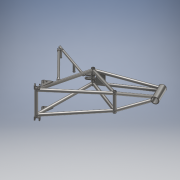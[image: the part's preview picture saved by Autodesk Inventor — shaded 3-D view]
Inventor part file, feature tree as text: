
AUTODESK INVENTOR PART (.ipt)
format: ipt  version: 2018 (Build 220112000, 112)  size: 1,016,832 bytes
history: native  units: mm
features: other x19, sketch x15, extrude x13, plane x10, loft x3, boolean_combine x2, thicken_offset x2, shell x1, mirror x1, hole x1, projected_geometry x1
ambient origin geometry x8: Origin, YZ Plane, XZ Plane, XY Plane, X Axis, Y Axis, Z Axis, Center Point
bodies: Solid8 (feature_tree), Solid1 (feature_tree), Solid16 (feature_tree), Solid17 (feature_tree), Solid18 (feature_tree), Solid19 (feature_tree), Solid20 (feature_tree), Solid24 (feature_tree)
feature tree (68):
  other  "MainFrame.ipt"
  plane  "Work Plane1"
  extrude  "Extrusion1"  Depth=10.0mm
  sketch  "3D Sketch3"
  plane  "Work Plane4"
  extrude  "Extrusion2"  Depth=13.0mm
  plane  "Work Plane5"
  extrude  "Extrusion4"  Depth=3.5mm
  loft  "Loft1"
  plane  "Work Plane2"
  extrude  "Extrusion5"  Depth=10.0mm TaperAngle=0.0deg
  extrude  "Extrusion6"  Depth=18.0mm TaperAngle=0.0deg
  shell  "Shell1"  Thickness=0.0mm
  plane  "Work Plane6"
  extrude  "Extrusion7"  Depth=5.0mm
  sketch  "3D Sketch4"
  plane  "Work Plane7"
  plane  "Work Plane8"
  plane  "Work Plane9"
  plane  "Work Plane11"
  extrude  "Extrusion8"  Depth=4.0mm TaperAngle=0.0deg
  extrude  "Extrusion9"  Depth=1.2mm
  extrude  "Extrusion10"  Depth=20.0mm
  loft  "Loft2"
  loft  "Loft3"
  extrude  "Extrusion13"  Depth=4.0mm TaperAngle=0.0deg
  extrude  "Extrusion15"  Depth=4.0mm TaperAngle=0.0deg
  mirror  "Mirror4"
  sketch  "Sketch17"  dims[d37=13.0mm d38=5.0mm d39=3.5mm d40=4.5mm d41=0.0mm d42=20.0mm]
  plane  "Work Plane13"
  sketch  "Sketch20"  dims[d43=20.0mm d44=-10.0mm d45=10.0mm]
  extrude  "Extrusion17"  Depth=4.0mm
  hole  "Hole3"  [1 undecoded]
  boolean_combine  "Combine2"
  thicken_offset  "Thicken2"
  extrude  "Extrusion19"  Depth=4.0mm TaperAngle=0.0deg
  boolean_combine  "Combine4"
  thicken_offset  "Thicken4"
  other  "Frame::MainFrame.ipt"
  other  "TaggingFeature1"
  sketch  "Sketch1"  dims[d0=10.0mm d1=50.0mm]
  other  "PlateA"
  sketch  "Sketch3"  dims[d2=37.0mm d3=13.0mm]
  sketch  "Sketch4"  dims[d4=5.0mm d5=3.5mm]
  other  "Edges1"
  other  "Edges2"
  sketch  "Sketch5"  dims[d6=4.4mm d7=0.0mm d8=20.0mm]
  other  "PlateB"
  sketch  "Sketch6"  dims[d11=15.875mm d13=10.0mm d14=0.0mm]
  sketch  "Sketch8"  dims[d15=-10.0mm d18=18.0mm d19=0.0mm d20=0.0mm d21=90.0deg]
  sketch  "Sketch9"  dims[d22=0.0mm d23=90.0deg d26=5.0mm]
  sketch  "Sketch10"  dims[d29=4.0mm d30=3.0mm d31=0.0mm]
  sketch  "Sketch11"  dims[d32=3.0mm d33=0.0mm d34=1.2mm]
  other  "Edges5"
  other  "Edges6"
  other  "Edges3"
  other  "Edges4"
  sketch  "Sketch16"  dims[d35=75.0mm]
  other  "SeatFrontFix"
  other  "PivotPlateRight::MainFrame.ipt"
  other  "ShockPlate::MainFrame.ipt"
  other  "PivotPlateLeft::MainFrame.ipt"
  other  "FootpegRight::MainFrame.ipt"
  other  "FootpegLeft::MainFrame.ipt"
  other  "HeadTube::MainFrame.ipt"
  sketch  "Sketch22"  dims[d46=18.0mm d47=0.0mm d48=15.875mm d49=4.5mm d50=0.0mm d51=18.0mm d52=0.0mm d53=0.0mm d54=90.0deg d55=0.0mm d56=90.0deg d57=0.0mm d58=90.0deg d59=0.0mm d60=90.0deg d65=15.875mm d66=1.2mm d67=132.0mm d68=0.0mm d71=15.875mm d72=1.2mm d74=10.0mm d75=0.0mm d77=300.0mm d99=10.0mm d100=0.0mm d101=8.0mm d102=6.0mm d103=4.0mm d104=2.0mm d105=90.0deg d106=8.0mm d107=20.594885mm d108=1.0mm d109=1.0mm d116=8.0mm d117=0.0mm d120=1.0mm d121=1.0mm]
  projected_geometry  "Projected Loop2"
  other  "SeatFrontFixUpper"
note: 1 required parameter value undecoded (feature->parameter linkage not recoverable at this tier; creation-order binding heuristic only, values carry confidence <= 0.55)
